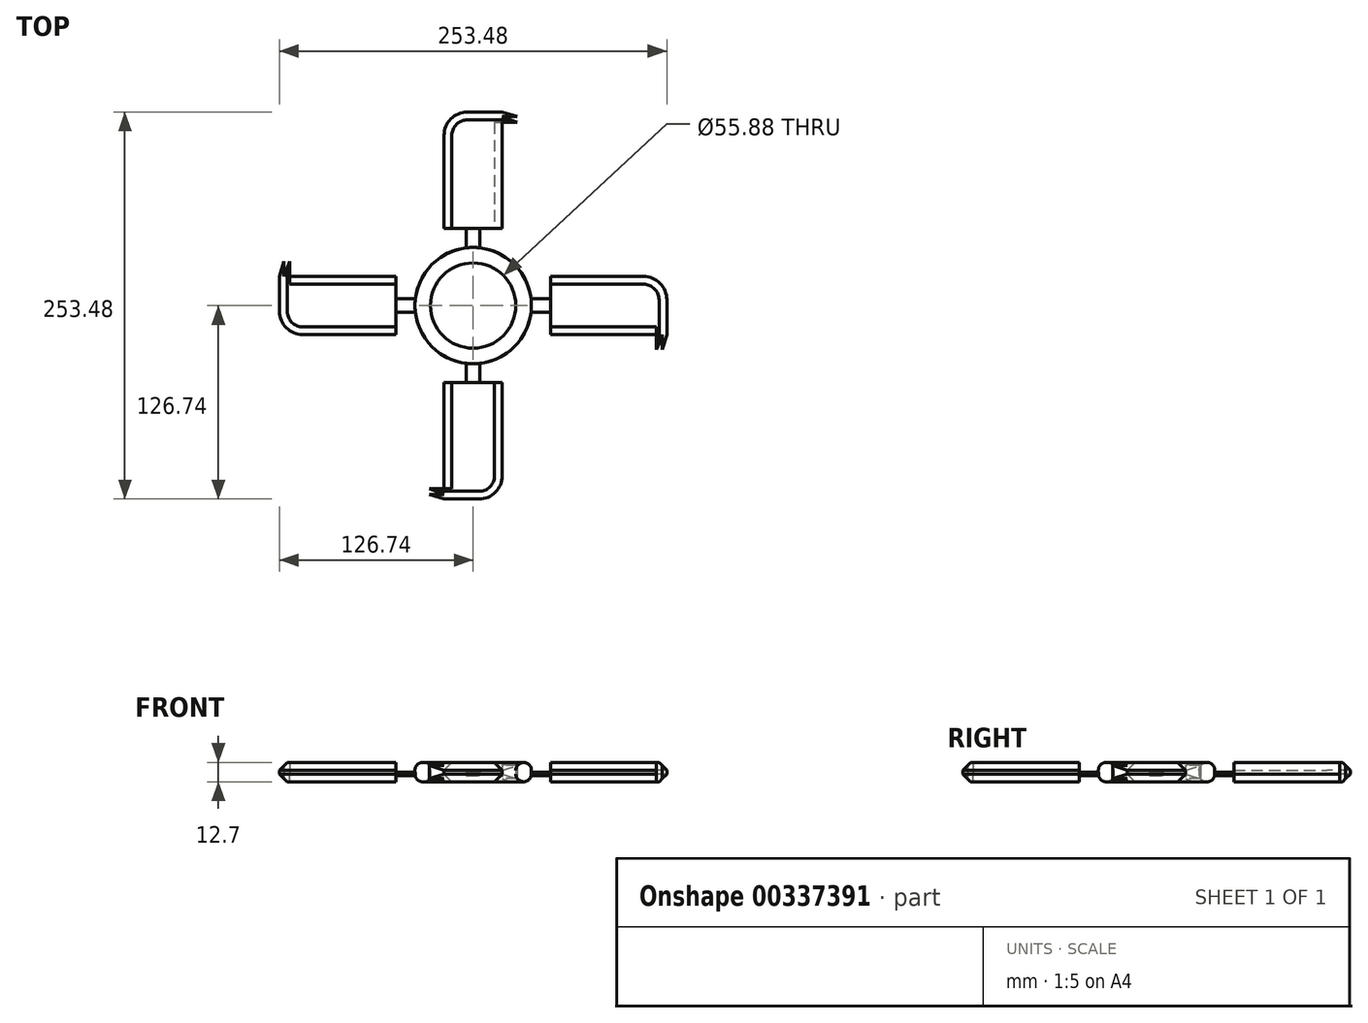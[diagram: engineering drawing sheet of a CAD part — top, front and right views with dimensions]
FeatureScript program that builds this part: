
annotation { "Feature Type Name" : "Feature", "Feature Type Description" : "" }
export const myFeature = defineFeature(function(context is Context, id is Id, definition is map)
    precondition{}
    {
        {
            var Q0;
            Q0=qCreatedBy(makeId("Top.planeOp"),FACE);
            var sketch = newSketch(context, id + "F0", { "sketchPlane" : qUnion([Q0])});
            skCircle(sketch, "E0", {"center": v(0, 0) * mm, "radius": 38.1 * mm});
            skCircle(sketch, "E1", {"center": v(0, 0) * mm, "radius": 27.94 * mm});
            skLineSegment(sketch, "E2", {"start": v(-37.84, 4.45) * mm, "end": v(-50.54, 4.44) * mm});
            skLineSegment(sketch, "E3", {"start": v(-37.84, -4.45) * mm, "end": v(-50.54, -4.45) * mm});
            skLineSegment(sketch, "E4", {"start": v(-4.45, 37.84) * mm, "end": v(-4.45, 50.54) * mm});
            skLineSegment(sketch, "E5", {"start": v(4.45, 37.84) * mm, "end": v(4.45, 50.54) * mm});
            skLineSegment(sketch, "E6", {"start": v(-4.44, -37.84) * mm, "end": v(-4.44, -50.54) * mm});
            skLineSegment(sketch, "E7", {"start": v(4.44, -37.84) * mm, "end": v(4.45, -50.54) * mm});
            skLineSegment(sketch, "E8", {"start": v(37.84, 4.45) * mm, "end": v(50.54, 4.45) * mm});
            skLineSegment(sketch, "E9", {"start": v(37.84, -4.45) * mm, "end": v(50.54, -4.45) * mm});
            skLineSegment(sketch, "E10", {"start": v(-4.45, 50.54) * mm, "end": v(4.45, 50.54) * mm});
            skLineSegment(sketch, "E11", {"start": v(50.54, 4.45) * mm, "end": v(50.54, -4.45) * mm});
            skLineSegment(sketch, "E12", {"start": v(4.45, -50.54) * mm, "end": v(-4.44, -50.54) * mm});
            skLineSegment(sketch, "E13", {"start": v(-50.54, -4.45) * mm, "end": v(-50.54, 4.44) * mm});
            skLineSegment(sketch, "E14", {"start": v(-50.54, 4.44) * mm, "end": v(-50.54, 19.05) * mm});
            skLineSegment(sketch, "E15", {"start": v(-50.54, -4.45) * mm, "end": v(-50.54, -19.05) * mm});
            skLineSegment(sketch, "E16", {"start": v(-4.44, -50.54) * mm, "end": v(-19.05, -50.54) * mm});
            skLineSegment(sketch, "E17", {"start": v(4.45, -50.54) * mm, "end": v(19.05, -50.54) * mm});
            skLineSegment(sketch, "E18", {"start": v(50.54, -4.45) * mm, "end": v(50.54, -19.05) * mm});
            skLineSegment(sketch, "E19", {"start": v(50.54, 19.05) * mm, "end": v(50.54, 4.44) * mm});
            skLineSegment(sketch, "E20", {"start": v(19.05, 50.54) * mm, "end": v(4.44, 50.54) * mm});
            skLineSegment(sketch, "E21", {"start": v(-19.05, 50.54) * mm, "end": v(-4.45, 50.54) * mm});
            skLineSegment(sketch, "E22.bottom", {"start": v(-19.05, -50.54) * mm, "end": v(19.05, -50.54) * mm});
            skLineSegment(sketch, "E22.top", {"start": v(-19.05, -126.74) * mm, "end": v(19.05, -126.74) * mm});
            skLineSegment(sketch, "E22.left", {"start": v(-19.05, -50.54) * mm, "end": v(-19.05, -126.74) * mm});
            skLineSegment(sketch, "E22.right", {"start": v(19.05, -50.54) * mm, "end": v(19.05, -126.74) * mm});
            skLineSegment(sketch, "E23", {"start": v(-19.05, -126.74) * mm, "end": v(-28.83, -123.78) * mm});
            skLineSegment(sketch, "E24", {"start": v(-28.83, -123.78) * mm, "end": v(-19.05, -123.78) * mm});
            skLineSegment(sketch, "E25", {"start": v(-19.05, -123.78) * mm, "end": v(-28.83, -119.97) * mm});
            skLineSegment(sketch, "E26", {"start": v(-28.83, -119.97) * mm, "end": v(-19.05, -119.97) * mm});
            skLineSegment(sketch, "E27.1.0", {"start": v(50.54, 19.05) * mm, "end": v(126.74, 19.05) * mm});
            skLineSegment(sketch, "E27.1.1", {"start": v(50.54, -19.05) * mm, "end": v(126.74, -19.05) * mm});
            skLineSegment(sketch, "E27.1.2", {"start": v(126.74, -19.05) * mm, "end": v(126.74, 19.05) * mm});
            skLineSegment(sketch, "E27.1.3", {"start": v(126.74, -19.05) * mm, "end": v(123.78, -28.83) * mm});
            skLineSegment(sketch, "E27.1.4", {"start": v(123.78, -28.83) * mm, "end": v(123.78, -19.05) * mm});
            skLineSegment(sketch, "E27.1.5", {"start": v(123.78, -19.05) * mm, "end": v(119.97, -28.83) * mm});
            skLineSegment(sketch, "E27.1.6", {"start": v(119.97, -28.83) * mm, "end": v(119.97, -19.05) * mm});
            skLineSegment(sketch, "E27.2.0", {"start": v(-19.05, 50.54) * mm, "end": v(-19.05, 126.74) * mm});
            skLineSegment(sketch, "E27.2.1", {"start": v(19.05, 50.54) * mm, "end": v(19.05, 126.74) * mm});
            skLineSegment(sketch, "E27.2.2", {"start": v(19.05, 126.74) * mm, "end": v(-19.05, 126.74) * mm});
            skLineSegment(sketch, "E27.2.3", {"start": v(19.05, 126.74) * mm, "end": v(28.83, 123.78) * mm});
            skLineSegment(sketch, "E27.2.4", {"start": v(28.83, 123.78) * mm, "end": v(19.05, 123.78) * mm});
            skLineSegment(sketch, "E27.2.5", {"start": v(19.05, 123.78) * mm, "end": v(28.83, 119.97) * mm});
            skLineSegment(sketch, "E27.2.6", {"start": v(28.83, 119.97) * mm, "end": v(19.05, 119.97) * mm});
            skLineSegment(sketch, "E27.3.0", {"start": v(-50.54, -19.05) * mm, "end": v(-126.74, -19.05) * mm});
            skLineSegment(sketch, "E27.3.1", {"start": v(-50.54, 19.05) * mm, "end": v(-126.74, 19.05) * mm});
            skLineSegment(sketch, "E27.3.2", {"start": v(-126.74, 19.05) * mm, "end": v(-126.74, -19.05) * mm});
            skLineSegment(sketch, "E27.3.3", {"start": v(-126.74, 19.05) * mm, "end": v(-123.78, 28.83) * mm});
            skLineSegment(sketch, "E27.3.4", {"start": v(-123.78, 28.83) * mm, "end": v(-123.78, 19.05) * mm});
            skLineSegment(sketch, "E27.3.5", {"start": v(-123.78, 19.05) * mm, "end": v(-119.97, 28.83) * mm});
            skLineSegment(sketch, "E27.3.6", {"start": v(-119.97, 28.83) * mm, "end": v(-119.97, 19.05) * mm});
            skSolve(sketch);
        }
        {
            var Q0;
            Q0=makeQuery(id+"F0.imprint","IMPRINT",FACE,{"disambiguationData":[TD([[makeQuery(id+"F0.imprint","IMPRINT",EDGE,{"derivedFrom":sQuery(id+"F0.wireOp",EDGE,"E13")}),1.0]])]});
            var Q1;
            Q1=makeQuery(id+"F0.imprint","IMPRINT",FACE,{"disambiguationData":[TD([[makeQuery(id+"F0.imprint","IMPRINT",EDGE,{"derivedFrom":sQuery(id+"F0.wireOp",EDGE,"E1")}),-1.0]])]});
            var Q2;
            Q2=makeQuery(id+"F0.imprint","IMPRINT",FACE,{"disambiguationData":[TD([[makeQuery(id+"F0.imprint","IMPRINT",EDGE,{"derivedFrom":sQuery(id+"F0.wireOp",EDGE,"E11")}),1.0]])]});
            var Q3;
            Q3=makeQuery(id+"F0.imprint","IMPRINT",FACE,{"disambiguationData":[TD([[makeQuery(id+"F0.imprint","IMPRINT",EDGE,{"derivedFrom":sQuery(id+"F0.wireOp",EDGE,"E10")}),1.0]])]});
            var Q4;
            {var subQ0=sQuery(id+"F0.wireOp",EDGE,"E22.top");Q4=makeQuery(id+"F0.imprint","IMPRINT",FACE,{"disambiguationData":[TD([[makeQuery(id+"F0.imprint","IMPRINT",EDGE,{"derivedFrom":subQ0}),1.0]])]});}
            var Q5;
            {var subQ0=sQuery(id+"F0.wireOp",EDGE,"E27.3.3");Q5=makeQuery(id+"F0.imprint","IMPRINT",FACE,{"disambiguationData":[TD([[makeQuery(id+"F0.imprint","IMPRINT",EDGE,{"derivedFrom":subQ0}),-1.0]])]});}
            var Q6;
            {var subQ0=sQuery(id+"F0.wireOp",EDGE,"E27.3.5");Q6=makeQuery(id+"F0.imprint","IMPRINT",FACE,{"disambiguationData":[TD([[makeQuery(id+"F0.imprint","IMPRINT",EDGE,{"derivedFrom":subQ0}),-1.0]])]});}
            var Q7;
            {var subQ0=sQuery(id+"F0.wireOp",EDGE,"E23");Q7=makeQuery(id+"F0.imprint","IMPRINT",FACE,{"disambiguationData":[TD([[makeQuery(id+"F0.imprint","IMPRINT",EDGE,{"derivedFrom":subQ0}),-1.0]])]});}
            var Q8;
            {var subQ0=sQuery(id+"F0.wireOp",EDGE,"E25");Q8=makeQuery(id+"F0.imprint","IMPRINT",FACE,{"disambiguationData":[TD([[makeQuery(id+"F0.imprint","IMPRINT",EDGE,{"derivedFrom":subQ0}),-1.0]])]});}
            var Q9;
            {var subQ0=sQuery(id+"F0.wireOp",EDGE,"E27.1.5");Q9=makeQuery(id+"F0.imprint","IMPRINT",FACE,{"disambiguationData":[TD([[makeQuery(id+"F0.imprint","IMPRINT",EDGE,{"derivedFrom":subQ0}),-1.0]])]});}
            var Q10;
            {var subQ0=sQuery(id+"F0.wireOp",EDGE,"E27.1.3");Q10=makeQuery(id+"F0.imprint","IMPRINT",FACE,{"disambiguationData":[TD([[makeQuery(id+"F0.imprint","IMPRINT",EDGE,{"derivedFrom":subQ0}),-1.0]])]});}
            var Q11;
            {var subQ0=sQuery(id+"F0.wireOp",EDGE,"E27.2.3");Q11=makeQuery(id+"F0.imprint","IMPRINT",FACE,{"disambiguationData":[TD([[makeQuery(id+"F0.imprint","IMPRINT",EDGE,{"derivedFrom":subQ0}),-1.0]])]});}
            var Q12;
            {var subQ0=sQuery(id+"F0.wireOp",EDGE,"E27.2.5");Q12=makeQuery(id+"F0.imprint","IMPRINT",FACE,{"disambiguationData":[TD([[makeQuery(id+"F0.imprint","IMPRINT",EDGE,{"derivedFrom":subQ0}),-1.0]])]});}
            extrude(context, id + "F1", {"entities" : qUnion([Q0, Q1, Q2, Q3, Q4, Q5, Q6, Q7, Q8, Q9, Q10, Q11, Q12]), "depth" : 12.7 * mm});
        }
        {
            var Q0;
            {var subQ0=sQuery(id+"F0.wireOp",EDGE,"E2");Q0=makeQuery(id+"F0.imprint","IMPRINT",FACE,{"disambiguationData":[TD([[makeQuery(id+"F0.imprint","IMPRINT",EDGE,{"derivedFrom":subQ0}),1.0]])]});}
            var Q1;
            {var subQ0=sQuery(id+"F0.wireOp",EDGE,"E4");Q1=makeQuery(id+"F0.imprint","IMPRINT",FACE,{"disambiguationData":[TD([[makeQuery(id+"F0.imprint","IMPRINT",EDGE,{"derivedFrom":subQ0}),-1.0]])]});}
            var Q2;
            {var subQ0=sQuery(id+"F0.wireOp",EDGE,"E8");Q2=makeQuery(id+"F0.imprint","IMPRINT",FACE,{"disambiguationData":[TD([[makeQuery(id+"F0.imprint","IMPRINT",EDGE,{"derivedFrom":subQ0}),-1.0]])]});}
            var Q3;
            {var subQ0=sQuery(id+"F0.wireOp",EDGE,"E6");Q3=makeQuery(id+"F0.imprint","IMPRINT",FACE,{"disambiguationData":[TD([[makeQuery(id+"F0.imprint","IMPRINT",EDGE,{"derivedFrom":subQ0}),1.0]])]});}
            extrude(context, id + "F2", {"entities" : qUnion([Q0, Q1, Q2, Q3]), "depth" : 6.35 * mm});
        }
        {
            var Q0;
            {var subQ0=sQuery(id+"F0.wireOp",EDGE,"E6");Q0=makeQuery(id+"F0.imprint","IMPRINT",FACE,{"disambiguationData":[TD([[makeQuery(id+"F0.imprint","IMPRINT",EDGE,{"derivedFrom":subQ0}),1.0]])]});}
            var Q1;
            {var subQ0=sQuery(id+"F0.wireOp",EDGE,"E8");Q1=makeQuery(id+"F0.imprint","IMPRINT",FACE,{"disambiguationData":[TD([[makeQuery(id+"F0.imprint","IMPRINT",EDGE,{"derivedFrom":subQ0}),-1.0]])]});}
            var Q2;
            {var subQ0=sQuery(id+"F0.wireOp",EDGE,"E4");Q2=makeQuery(id+"F0.imprint","IMPRINT",FACE,{"disambiguationData":[TD([[makeQuery(id+"F0.imprint","IMPRINT",EDGE,{"derivedFrom":subQ0}),-1.0]])]});}
            var Q3;
            {var subQ0=sQuery(id+"F0.wireOp",EDGE,"E2");Q3=makeQuery(id+"F0.imprint","IMPRINT",FACE,{"disambiguationData":[TD([[makeQuery(id+"F0.imprint","IMPRINT",EDGE,{"derivedFrom":subQ0}),1.0]])]});}
            extrude(context, id + "F3", {"entities" : qUnion([Q0, Q1, Q2, Q3]), "operationType" : NewBodyOperationType.REMOVE, "depth" : 3.94 * mm});
        }
        {
            var Q0;
            Q0=makeQuery(id+"F1.opExtrude","SWEPT_EDGE",EDGE,{"disambiguationData":[OSD([sQuery(id+"F0.wireOp",EDGE,"E27.1.0"),sQuery(id+"F0.wireOp",EDGE,"E27.1.2")])]});
            var Q1;
            Q1=makeQuery(id+"F1.opExtrude","SWEPT_EDGE",EDGE,{"disambiguationData":[OSD([sQuery(id+"F0.wireOp",EDGE,"E22.top"),sQuery(id+"F0.wireOp",EDGE,"E22.right")])]});
            var Q2;
            Q2=makeQuery(id+"F1.opExtrude","SWEPT_EDGE",EDGE,{"disambiguationData":[OSD([sQuery(id+"F0.wireOp",EDGE,"E27.2.0"),sQuery(id+"F0.wireOp",EDGE,"E27.2.2")])]});
            var Q3;
            Q3=makeQuery(id+"F1.opExtrude","SWEPT_EDGE",EDGE,{"disambiguationData":[OSD([sQuery(id+"F0.wireOp",EDGE,"E27.3.0"),sQuery(id+"F0.wireOp",EDGE,"E27.3.2")])]});
            fillet(context, id + "F4", {"entities" : qUnion([Q0, Q1, Q2, Q3]), "radius" : 15.24 * mm, "tangentPropagation" : true, "allowEdgeOverflow" : false});
        }
        {
            var Q0;
            Q0=makeQuery(id+"F1.opExtrude","CAP_EDGE",EDGE,{"disambiguationData":[OSD([sQuery(id+"F0.wireOp",EDGE,"E27.1.0")])],"isStart":false});
            var Q1;
            Q1=makeQuery(id+"F1.opExtrude","CAP_EDGE",EDGE,{"disambiguationData":[OSD([sQuery(id+"F0.wireOp",EDGE,"E27.1.0")])],"isStart":true});
            var Q2;
            Q2=makeQuery(id+"F1.opExtrude","CAP_EDGE",EDGE,{"disambiguationData":[OSD([sQuery(id+"F0.wireOp",EDGE,"E27.2.2")])],"isStart":false});
            var Q3;
            Q3=makeQuery(id+"F1.opExtrude","CAP_EDGE",EDGE,{"disambiguationData":[OSD([sQuery(id+"F0.wireOp",EDGE,"E27.2.0")])],"isStart":true});
            var Q4;
            Q4=makeQuery(id+"F1.opExtrude","CAP_EDGE",EDGE,{"disambiguationData":[OSD([sQuery(id+"F0.wireOp",EDGE,"E27.2.1")])],"isStart":true});
            var Q5;
            Q5=makeQuery(id+"F1.opExtrude","CAP_EDGE",EDGE,{"disambiguationData":[OSD([sQuery(id+"F0.wireOp",EDGE,"E27.1.1")])],"isStart":true});
            var Q6;
            Q6=makeQuery(id+"F1.opExtrude","CAP_EDGE",EDGE,{"disambiguationData":[OSD([sQuery(id+"F0.wireOp",EDGE,"E27.1.1")])],"isStart":false});
            var Q7;
            Q7=makeQuery(id+"F1.opExtrude","CAP_EDGE",EDGE,{"disambiguationData":[OSD([sQuery(id+"F0.wireOp",EDGE,"E27.3.1")])],"isStart":true});
            var Q8;
            Q8=makeQuery(id+"F1.opExtrude","CAP_EDGE",EDGE,{"disambiguationData":[OSD([sQuery(id+"F0.wireOp",EDGE,"E27.3.0")])],"isStart":true});
            var Q9;
            Q9=makeQuery(id+"F1.opExtrude","CAP_EDGE",EDGE,{"disambiguationData":[OSD([sQuery(id+"F0.wireOp",EDGE,"E27.3.0")])],"isStart":false});
            var Q10;
            Q10=makeQuery(id+"F1.opExtrude","CAP_EDGE",EDGE,{"disambiguationData":[OSD([sQuery(id+"F0.wireOp",EDGE,"E22.left")])],"isStart":true});
            var Q11;
            Q11=makeQuery(id+"F1.opExtrude","CAP_EDGE",EDGE,{"disambiguationData":[OSD([sQuery(id+"F0.wireOp",EDGE,"E22.right")])],"isStart":true});
            var Q12;
            Q12=makeQuery(id+"F1.opExtrude","CAP_EDGE",EDGE,{"disambiguationData":[OSD([sQuery(id+"F0.wireOp",EDGE,"E22.right")])],"isStart":false});
            var Q13;
            Q13=makeQuery(id+"F1.opExtrude","CAP_EDGE",EDGE,{"disambiguationData":[OSD([sQuery(id+"F0.wireOp",EDGE,"E22.left")])],"isStart":false});
            var Q14;
            Q14=makeQuery(id+"F1.opExtrude","CAP_EDGE",EDGE,{"disambiguationData":[OSD([sQuery(id+"F0.wireOp",EDGE,"E27.3.1")])],"isStart":false});
            chamfer(context, id + "F5", {"entities" : qUnion([Q0, Q1, Q2, Q3, Q4, Q5, Q6, Q7, Q8, Q9, Q10, Q11, Q12, Q13, Q14]), "width" : 5.08 * mm, "tangentPropagation" : true});
        }
        {
            var Q0;
            Q0=makeQuery(id+"F1.opExtrude","CAP_EDGE",EDGE,{"disambiguationData":[OSD([sQuery(id+"F0.wireOp",EDGE,"E1")])],"isStart":false});
            var Q1;
            Q1=makeQuery(id+"F1.opExtrude","CAP_EDGE",EDGE,{"disambiguationData":[OSD([sQuery(id+"F0.wireOp",EDGE,"E0")])],"isStart":false});
            var Q2;
            Q2=makeQuery(id+"F1.opExtrude","CAP_EDGE",EDGE,{"disambiguationData":[OSD([sQuery(id+"F0.wireOp",EDGE,"E0")])],"isStart":true});
            var Q3;
            Q3=makeQuery(id+"F1.opExtrude","CAP_EDGE",EDGE,{"disambiguationData":[OSD([sQuery(id+"F0.wireOp",EDGE,"E1")])],"isStart":true});
            fillet(context, id + "F6", {"entities" : qUnion([Q0, Q1, Q2, Q3]), "radius" : 5.08 * mm, "tangentPropagation" : true, "allowEdgeOverflow" : false});
        }
    });
